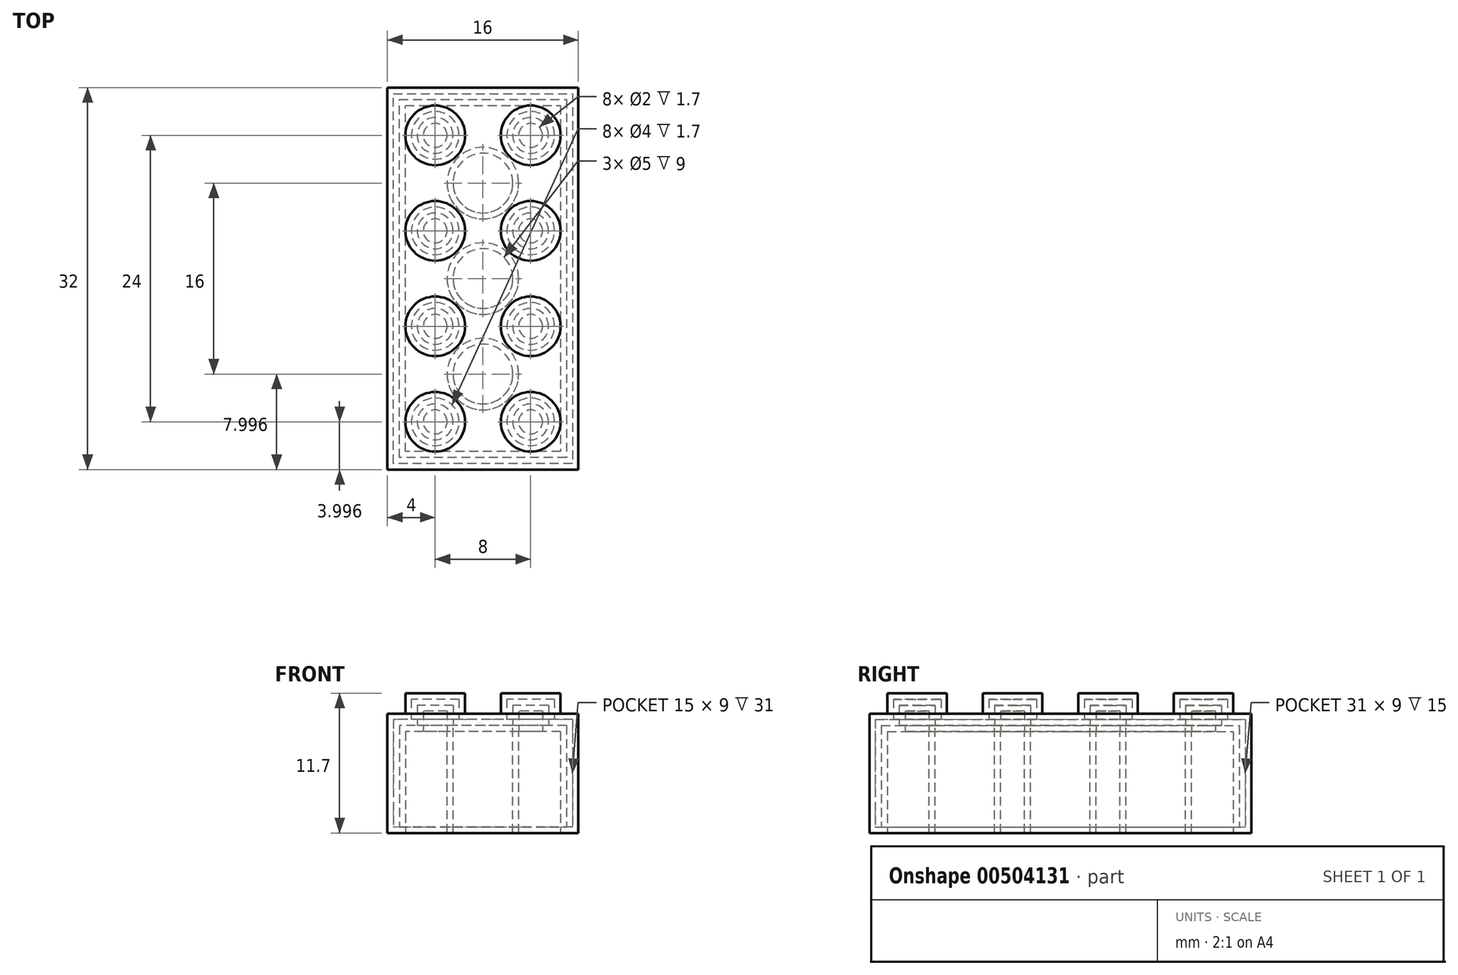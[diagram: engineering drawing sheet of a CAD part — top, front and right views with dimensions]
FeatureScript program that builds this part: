
annotation { "Feature Type Name" : "Feature", "Feature Type Description" : "" }
export const myFeature = defineFeature(function(context is Context, id is Id, definition is map)
    precondition{}
    {
        {
            var Q0;
            Q0=qCreatedBy(makeId("Top.planeOp"),FACE);
            var sketch = newSketch(context, id + "F0", { "sketchPlane" : qUnion([Q0])});
            skLineSegment(sketch, "E0", {"start": v(0, -74.61) * mm, "end": v(0, -42.61) * mm});
            skLineSegment(sketch, "E1", {"start": v(0, -42.61) * mm, "end": v(16, -42.61) * mm});
            skLineSegment(sketch, "E2", {"start": v(16, -42.61) * mm, "end": v(16, -74.61) * mm});
            skLineSegment(sketch, "E3", {"start": v(16, -74.61) * mm, "end": v(0, -74.61) * mm});
            skSolve(sketch);
        }
        {
            var Q0;
            Q0=makeQuery(id+"F0.imprint","IMPRINT",FACE,{"disambiguationData":[TD([[makeQuery(id+"F0.imprint","IMPRINT",EDGE,{"derivedFrom":sQuery(id+"F0.wireOp",EDGE,"E0")}),-1.0]])]});
            extrude(context, id + "F1", {"entities" : qUnion([Q0]), "depth" : 10 * mm});
        }
        {
            var Q0;
            Q0=makeQuery(id+"F1.opExtrude","CAP_FACE",FACE,{"disambiguationData":[OSD([sQuery(id+"F0.wireOp",EDGE,"E0"),sQuery(id+"F0.wireOp",EDGE,"E1"),sQuery(id+"F0.wireOp",EDGE,"E2"),sQuery(id+"F0.wireOp",EDGE,"E3")])],"isStart":false});
            var sketch = newSketch(context, id + "F2", { "sketchPlane" : qUnion([Q0])});
            skLineSegment(sketch, "E4", {"start": v(8, -42.61) * mm, "end": v(8, -46.61) * mm});
            skLineSegment(sketch, "E5", {"start": v(8, -46.61) * mm, "end": v(8, -54.61) * mm});
            skLineSegment(sketch, "E6", {"start": v(8, -74.61) * mm, "end": v(8, -70.61) * mm});
            skLineSegment(sketch, "E7", {"start": v(8, -70.61) * mm, "end": v(8, -62.61) * mm});
            skCircle(sketch, "E8", {"center": v(12, -70.61) * mm, "radius": 2.5 * mm});
            skCircle(sketch, "E9", {"center": v(4, -70.61) * mm, "radius": 2.5 * mm});
            skCircle(sketch, "E10", {"center": v(12, -62.61) * mm, "radius": 2.5 * mm});
            skCircle(sketch, "E11", {"center": v(12, -54.61) * mm, "radius": 2.5 * mm});
            skCircle(sketch, "E12", {"center": v(4, -54.61) * mm, "radius": 2.5 * mm});
            skCircle(sketch, "E13", {"center": v(4, -62.61) * mm, "radius": 2.5 * mm});
            skCircle(sketch, "E14", {"center": v(12, -46.61) * mm, "radius": 2.5 * mm});
            skCircle(sketch, "E15", {"center": v(4, -46.61) * mm, "radius": 2.5 * mm});
            skSolve(sketch);
        }
        {
            var Q0;
            Q0=makeQuery(id+"F2.imprint","IMPRINT",FACE,{"disambiguationData":[TD([[makeQuery(id+"F2.imprint","IMPRINT",EDGE,{"derivedFrom":sQuery(id+"F2.wireOp",EDGE,"E15")}),1.0]])]});
            var Q1;
            Q1=makeQuery(id+"F2.imprint","IMPRINT",FACE,{"disambiguationData":[TD([[makeQuery(id+"F2.imprint","IMPRINT",EDGE,{"derivedFrom":sQuery(id+"F2.wireOp",EDGE,"E12")}),1.0]])]});
            var Q2;
            Q2=makeQuery(id+"F2.imprint","IMPRINT",FACE,{"disambiguationData":[TD([[makeQuery(id+"F2.imprint","IMPRINT",EDGE,{"derivedFrom":sQuery(id+"F2.wireOp",EDGE,"E13")}),1.0]])]});
            var Q3;
            Q3=makeQuery(id+"F2.imprint","IMPRINT",FACE,{"disambiguationData":[TD([[makeQuery(id+"F2.imprint","IMPRINT",EDGE,{"derivedFrom":sQuery(id+"F2.wireOp",EDGE,"E9")}),1.0]])]});
            var Q4;
            Q4=makeQuery(id+"F2.imprint","IMPRINT",FACE,{"disambiguationData":[TD([[makeQuery(id+"F2.imprint","IMPRINT",EDGE,{"derivedFrom":sQuery(id+"F2.wireOp",EDGE,"E8")}),1.0]])]});
            var Q5;
            Q5=makeQuery(id+"F2.imprint","IMPRINT",FACE,{"disambiguationData":[TD([[makeQuery(id+"F2.imprint","IMPRINT",EDGE,{"derivedFrom":sQuery(id+"F2.wireOp",EDGE,"E10")}),1.0]])]});
            var Q6;
            Q6=makeQuery(id+"F2.imprint","IMPRINT",FACE,{"disambiguationData":[TD([[makeQuery(id+"F2.imprint","IMPRINT",EDGE,{"derivedFrom":sQuery(id+"F2.wireOp",EDGE,"E11")}),1.0]])]});
            var Q7;
            Q7=makeQuery(id+"F2.imprint","IMPRINT",FACE,{"disambiguationData":[TD([[makeQuery(id+"F2.imprint","IMPRINT",EDGE,{"derivedFrom":sQuery(id+"F2.wireOp",EDGE,"E14")}),1.0]])]});
            extrude(context, id + "F3", {"entities" : qUnion([Q0, Q1, Q2, Q3, Q4, Q5, Q6, Q7]), "operationType" : NewBodyOperationType.ADD, "depth" : 1.7 * mm});
        }
        {
            var Q0;
            Q0=makeQuery(id+"F1.opExtrude","CAP_FACE",FACE,{"disambiguationData":[OSD([sQuery(id+"F0.wireOp",EDGE,"E0"),sQuery(id+"F0.wireOp",EDGE,"E1"),sQuery(id+"F0.wireOp",EDGE,"E2"),sQuery(id+"F0.wireOp",EDGE,"E3")])],"isStart":true});
            shell(context, id + "F4", {"entities" : qUnion([Q0]), "thickness" : 1.5 * mm});
        }
        {
            var Q0;
            Q0=makeQuery(id+"F4.opShell","OFFSET_FACE",FACE,{"disambiguationData":[OSD([sQuery(id+"F0.wireOp",EDGE,"E0"),sQuery(id+"F0.wireOp",EDGE,"E1"),sQuery(id+"F0.wireOp",EDGE,"E2"),sQuery(id+"F0.wireOp",EDGE,"E3")])]});
            var sketch = newSketch(context, id + "F5", { "sketchPlane" : qUnion([Q0])});
            skPoint(sketch, "E16.endSnap0", {"position": v(14.5, 58.61) * mm});
            skPoint(sketch, "E17.endSnap0", {"position": v(8, 73.11) * mm});
            skPoint(sketch, "E18.endSnap0", {"position": v(8, 44.11) * mm});
            skCircle(sketch, "E19", {"center": v(8, 66.61) * mm, "radius": 3 * mm});
            skCircle(sketch, "E20", {"center": v(8, 58.61) * mm, "radius": 3 * mm});
            skCircle(sketch, "E21", {"center": v(8, 50.61) * mm, "radius": 3 * mm});
            skSolve(sketch);
        }
        {
            var Q0;
            Q0=makeQuery(id+"F5.imprint","IMPRINT",FACE,{"disambiguationData":[TD([[makeQuery(id+"F5.imprint","IMPRINT",EDGE,{"derivedFrom":sQuery(id+"F5.wireOp",EDGE,"E19")}),1.0]])]});
            var Q1;
            Q1=makeQuery(id+"F5.imprint","IMPRINT",FACE,{"disambiguationData":[TD([[makeQuery(id+"F5.imprint","IMPRINT",EDGE,{"derivedFrom":sQuery(id+"F5.wireOp",EDGE,"E20")}),1.0]])]});
            var Q2;
            Q2=makeQuery(id+"F5.imprint","IMPRINT",FACE,{"disambiguationData":[TD([[makeQuery(id+"F5.imprint","IMPRINT",EDGE,{"derivedFrom":sQuery(id+"F5.wireOp",EDGE,"E21")}),1.0]])]});
            extrude(context, id + "F6", {"entities" : qUnion([Q0, Q1, Q2]), "operationType" : NewBodyOperationType.ADD, "depth" : 8.5 * mm});
        }
        {
            var Q0;
            Q0=makeQuery(id+"F6.opExtrude","CAP_FACE",FACE,{"disambiguationData":[OSD([sQuery(id+"F5.wireOp",EDGE,"E19")])],"isStart":false});
            var Q1;
            Q1=makeQuery(id+"F6.opExtrude","CAP_FACE",FACE,{"disambiguationData":[OSD([sQuery(id+"F5.wireOp",EDGE,"E20")])],"isStart":false});
            var Q2;
            Q2=makeQuery(id+"F6.opExtrude","CAP_FACE",FACE,{"disambiguationData":[OSD([sQuery(id+"F5.wireOp",EDGE,"E21")])],"isStart":false});
            shell(context, id + "F7", {"entities" : qUnion([Q0, Q1, Q2]), "thickness" : 0.5 * mm});
        }
    });
